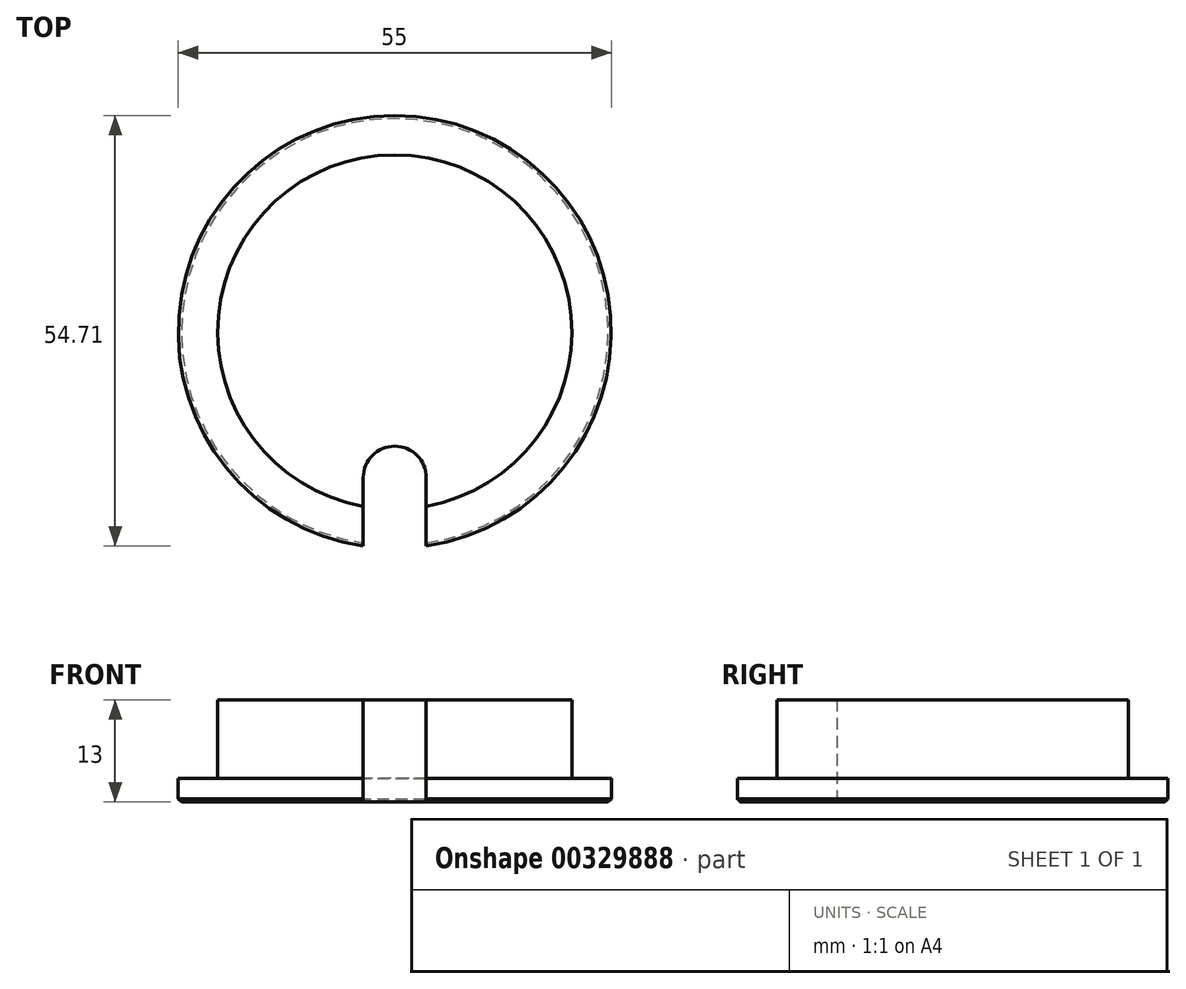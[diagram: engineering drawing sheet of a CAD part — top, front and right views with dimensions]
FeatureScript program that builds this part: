
annotation { "Feature Type Name" : "Feature", "Feature Type Description" : "" }
export const myFeature = defineFeature(function(context is Context, id is Id, definition is map)
    precondition{}
    {
        {
            var Q0;
            Q0=qCreatedBy(makeId("Top.planeOp"),FACE);
            var sketch = newSketch(context, id + "F0", { "sketchPlane" : qUnion([Q0])});
            skCircle(sketch, "E0", {"center": v(0, 0) * mm, "radius": 22.5 * mm});
            skSolve(sketch);
        }
        {
            var Q0;
            Q0 = qSketchRegion(id + "F0", true);
            extrude(context, id + "F1", {"entities" : qUnion([Q0]), "depth" : 10 * mm, "offsetDistance" : 25 * mm});
        }
        {
            var Q0;
            Q0=makeQuery(id+"F1.opExtrude","CAP_FACE",FACE,{"disambiguationData":[OSD([sQuery(id+"F0.wireOp",EDGE,"E0")])],"isStart":true});
            var sketch = newSketch(context, id + "F2", { "sketchPlane" : qUnion([Q0])});
            skCircle(sketch, "E1", {"center": v(0, 0) * mm, "radius": 27.5 * mm});
            skSolve(sketch);
        }
        {
            var Q0;
            Q0 = qSketchRegion(id + "F2", true);
            extrude(context, id + "F3", {"entities" : qUnion([Q0]), "operationType" : NewBodyOperationType.ADD, "depth" : 3 * mm, "offsetDistance" : 25 * mm});
        }
        {
            var Q0;
            Q0=makeQuery(id+"F3.opExtrude","CAP_EDGE",EDGE,{"disambiguationData":[OSD([sQuery(id+"F2.wireOp",EDGE,"E1")])],"isStart":false});
            chamfer(context, id + "F4", {"entities" : qUnion([Q0]), "width" : 0.4 * mm, "tangentPropagation" : true});
        }
        {
            var Q0;
            Q0=makeQuery(id+"F1.opExtrude","CAP_FACE",FACE,{"disambiguationData":[OSD([sQuery(id+"F0.wireOp",EDGE,"E0")])],"isStart":false});
            var sketch = newSketch(context, id + "F5", { "sketchPlane" : qUnion([Q0])});
            skArc(sketch, "E2", {"start": v(4, -18.5) * mm, "mid": v(0, -14.5) * mm, "end": v(-4, -18.5) * mm});
            skLineSegment(sketch, "E3", {"start": v(-4, -18.5) * mm, "end": v(-4, -27.2) * mm});
            skLineSegment(sketch, "E4", {"start": v(4, -18.5) * mm, "end": v(4, -27.2) * mm});
            skArc(sketch, "E5", {"start": v(-4, -27.2) * mm, "mid": v(0, -27.5) * mm, "end": v(4, -27.2) * mm});
            skSolve(sketch);
        }
        {
            var Q0;
            Q0 = qSketchRegion(id + "F5", true);
            extrude(context, id + "F6", {"entities" : qUnion([Q0]), "operationType" : NewBodyOperationType.REMOVE, "oppositeDirection" : true, "depth" : 25 * mm, "offsetDistance" : 25 * mm});
        }
    });
